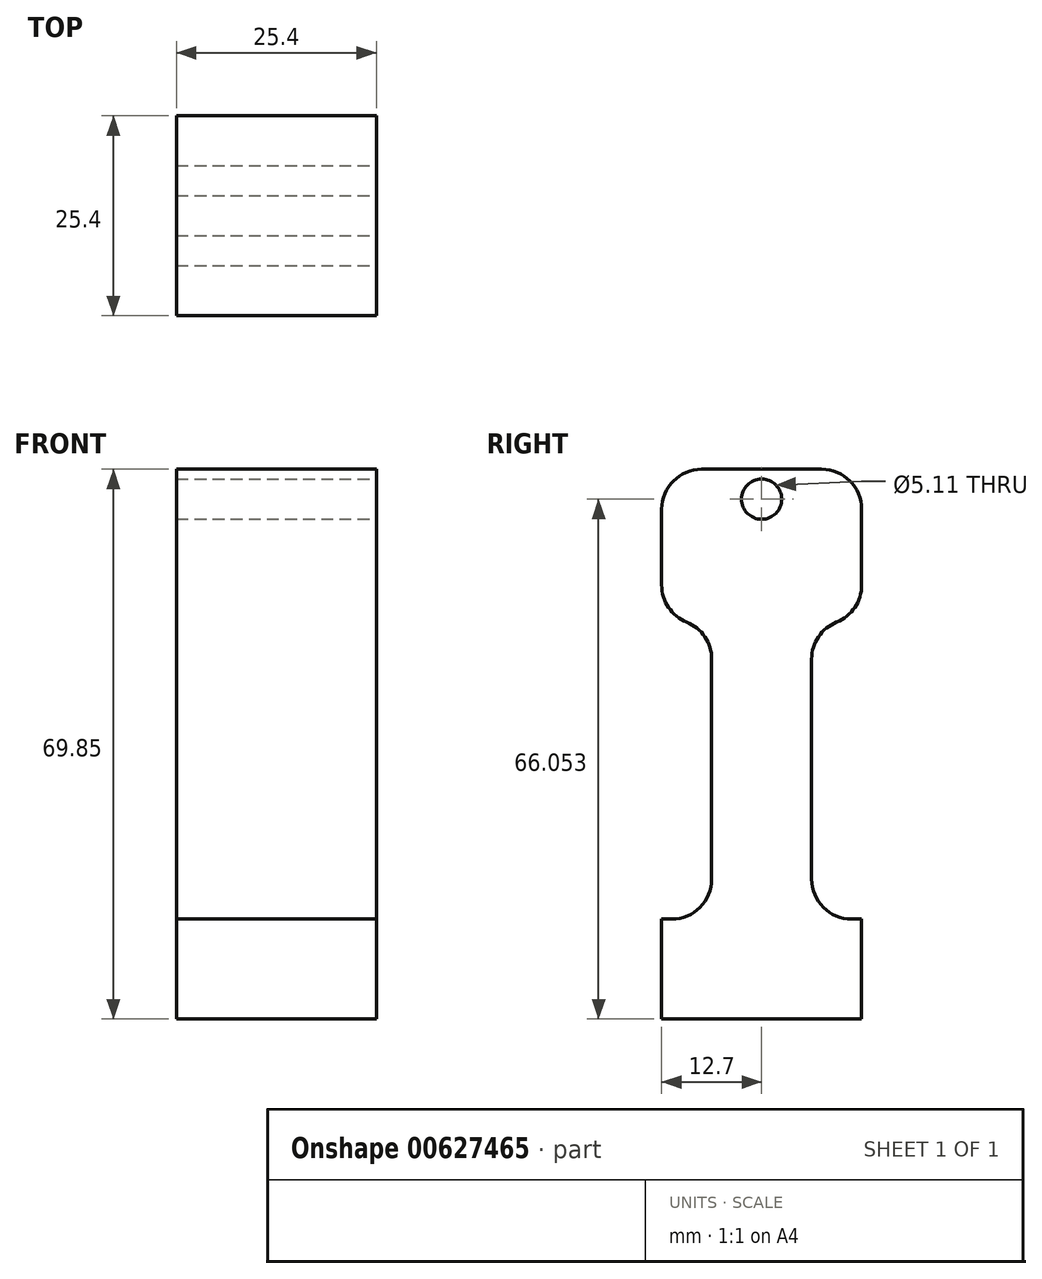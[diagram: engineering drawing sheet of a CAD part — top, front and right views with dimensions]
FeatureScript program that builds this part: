
annotation { "Feature Type Name" : "Feature", "Feature Type Description" : "" }
export const myFeature = defineFeature(function(context is Context, id is Id, definition is map)
    precondition{}
    {
        {
            var Q0;
            Q0=qCreatedBy(makeId("Top.planeOp"),FACE);
            var sketch = newSketch(context, id + "F0", { "sketchPlane" : qUnion([Q0])});
            skLineSegment(sketch, "E0.bottom", {"start": v(12.7, 12.7) * mm, "end": v(-12.7, 12.7) * mm});
            skLineSegment(sketch, "E0.top", {"start": v(12.7, -12.7) * mm, "end": v(-12.7, -12.7) * mm});
            skLineSegment(sketch, "E0.left", {"start": v(12.7, 12.7) * mm, "end": v(12.7, -12.7) * mm});
            skLineSegment(sketch, "E0.right", {"start": v(-12.7, 12.7) * mm, "end": v(-12.7, -12.7) * mm});
            skPoint(sketch, "E0.middle", {"position": v(0, 0) * mm});
            skSolve(sketch);
        }
        {
            var Q0;
            Q0 = qSketchRegion(id + "F0", true);
            extrude(context, id + "F1", {"entities" : qUnion([Q0]), "depth" : 69.85 * mm, "offsetDistance" : 25.4 * mm});
        }
        {
            var Q0;
            Q0=makeQuery(id+"F1.opExtrude","SWEPT_FACE",FACE,{"disambiguationData":[OSD([sQuery(id+"F0.wireOp",EDGE,"E0.left")])]});
            var sketch = newSketch(context, id + "F2", { "sketchPlane" : qUnion([Q0])});
            skCircle(sketch, "E1", {"center": v(0, 66.05) * mm, "radius": 2.55 * mm});
            skSolve(sketch);
        }
        {
            var Q0;
            Q0=makeQuery(id+"F2.imprint","IMPRINT",FACE,{"disambiguationData":[TD([[makeQuery(id+"F2.imprint","IMPRINT",EDGE,{"derivedFrom":sQuery(id+"F2.wireOp",EDGE,"E1")}),1.0]])]});
            extrude(context, id + "F3", {"entities" : qUnion([Q0]), "operationType" : NewBodyOperationType.REMOVE, "oppositeDirection" : true, "depth" : 25.4 * mm, "offsetDistance" : 25.4 * mm});
        }
        {
            var Q0;
            Q0=makeQuery(id+"F1.opExtrude","CAP_EDGE",EDGE,{"disambiguationData":[OSD([sQuery(id+"F0.wireOp",EDGE,"E0.top")])],"isStart":false});
            var Q1;
            Q1=makeQuery(id+"F1.opExtrude","CAP_EDGE",EDGE,{"disambiguationData":[OSD([sQuery(id+"F0.wireOp",EDGE,"E0.bottom")])],"isStart":false});
            fillet(context, id + "F4", {"entities" : qUnion([Q0, Q1]), "radius" : 5.08 * mm, "tangentPropagation" : true, "allowEdgeOverflow" : false});
        }
        {
            var Q0;
            Q0=makeQuery(id+"F1.opExtrude","SWEPT_FACE",FACE,{"disambiguationData":[OSD([sQuery(id+"F0.wireOp",EDGE,"E0.left")])]});
            var sketch = newSketch(context, id + "F5", { "sketchPlane" : qUnion([Q0])});
            skLineSegment(sketch, "E2.bottom", {"start": v(-12.7, 12.7) * mm, "end": v(-6.35, 12.7) * mm});
            skLineSegment(sketch, "E2.top", {"start": v(-12.7, 50.8) * mm, "end": v(-6.35, 50.8) * mm});
            skLineSegment(sketch, "E2.left", {"start": v(-12.7, 12.7) * mm, "end": v(-12.7, 50.8) * mm});
            skLineSegment(sketch, "E2.right", {"start": v(-6.35, 12.7) * mm, "end": v(-6.35, 50.8) * mm});
            skLineSegment(sketch, "E3.bottom", {"start": v(12.7, 12.7) * mm, "end": v(6.35, 12.7) * mm});
            skLineSegment(sketch, "E3.top", {"start": v(12.7, 50.8) * mm, "end": v(6.35, 50.8) * mm});
            skLineSegment(sketch, "E3.left", {"start": v(12.7, 12.7) * mm, "end": v(12.7, 50.8) * mm});
            skLineSegment(sketch, "E3.right", {"start": v(6.35, 12.7) * mm, "end": v(6.35, 50.8) * mm});
            skSolve(sketch);
        }
        {
            var Q0;
            Q0 = qSketchRegion(id + "F5", true);
            extrude(context, id + "F6", {"entities" : qUnion([Q0]), "operationType" : NewBodyOperationType.REMOVE, "oppositeDirection" : true, "depth" : 25.4 * mm, "offsetDistance" : 25.4 * mm});
        }
        {
            var Q0;
            Q0=makeQuery(id+"F6.boolean.opBoolean","COPY",EDGE,{"derivedFrom":makeQuery(id+"F6.opExtrude","SWEPT_EDGE",EDGE,{"disambiguationData":[OSD([sQuery(id+"F5.wireOp",EDGE,"E3.top"),sQuery(id+"F5.wireOp",EDGE,"E3.right")])]})});
            var Q1;
            Q1=makeQuery(id+"F6.boolean.opBoolean","COPY",EDGE,{"derivedFrom":makeQuery(id+"F6.opExtrude","SWEPT_EDGE",EDGE,{"disambiguationData":[OSD([sQuery(id+"F5.wireOp",EDGE,"E3.bottom"),sQuery(id+"F5.wireOp",EDGE,"E3.right")])]})});
            var Q2;
            Q2=makeQuery(id+"F6.boolean.opBoolean","COPY",EDGE,{"derivedFrom":makeQuery(id+"F6.opExtrude","SWEPT_EDGE",EDGE,{"disambiguationData":[OSD([sQuery(id+"F5.wireOp",EDGE,"E2.top"),sQuery(id+"F5.wireOp",EDGE,"E2.right")])]})});
            var Q3;
            Q3=makeQuery(id+"F6.boolean.opBoolean","COPY",EDGE,{"derivedFrom":makeQuery(id+"F6.opExtrude","SWEPT_EDGE",EDGE,{"disambiguationData":[OSD([sQuery(id+"F5.wireOp",EDGE,"E2.bottom"),sQuery(id+"F5.wireOp",EDGE,"E2.right")])]})});
            fillet(context, id + "F7", {"entities" : qUnion([Q0, Q1, Q2, Q3]), "radius" : 5.08 * mm, "tangentPropagation" : true, "allowEdgeOverflow" : false});
        }
        {
            var Q0;
            Q0=makeQuery(id+"F6.boolean.opBoolean","COPY",EDGE,{"derivedFrom":makeQuery(id+"F6.opExtrude","SWEPT_EDGE",EDGE,{"disambiguationData":[OSD([sQuery(id+"F0.wireOp",EDGE,"E0.top"),sQuery(id+"F0.wireOp",EDGE,"E0.left"),sQuery(id+"F5.wireOp",EDGE,"E2.bottom"),sQuery(id+"F5.wireOp",EDGE,"E2.left")])]})});
            var Q1;
            Q1=makeQuery(id+"F6.boolean.opBoolean","COPY",EDGE,{"derivedFrom":makeQuery(id+"F6.opExtrude","SWEPT_EDGE",EDGE,{"disambiguationData":[OSD([sQuery(id+"F0.wireOp",EDGE,"E0.top"),sQuery(id+"F0.wireOp",EDGE,"E0.left"),sQuery(id+"F5.wireOp",EDGE,"E2.top"),sQuery(id+"F5.wireOp",EDGE,"E2.left")])]})});
            var Q2;
            Q2=makeQuery(id+"F6.boolean.opBoolean","COPY",EDGE,{"derivedFrom":makeQuery(id+"F6.opExtrude","SWEPT_EDGE",EDGE,{"disambiguationData":[OSD([sQuery(id+"F0.wireOp",EDGE,"E0.bottom"),sQuery(id+"F0.wireOp",EDGE,"E0.left"),sQuery(id+"F5.wireOp",EDGE,"E3.bottom"),sQuery(id+"F5.wireOp",EDGE,"E3.left")])]})});
            var Q3;
            Q3=makeQuery(id+"F6.boolean.opBoolean","COPY",EDGE,{"derivedFrom":makeQuery(id+"F6.opExtrude","SWEPT_EDGE",EDGE,{"disambiguationData":[OSD([sQuery(id+"F0.wireOp",EDGE,"E0.bottom"),sQuery(id+"F0.wireOp",EDGE,"E0.left"),sQuery(id+"F5.wireOp",EDGE,"E3.top"),sQuery(id+"F5.wireOp",EDGE,"E3.left")])]})});
            fillet(context, id + "F8", {"entities" : qUnion([Q0, Q1, Q2, Q3]), "radius" : 5.08 * mm, "tangentPropagation" : true, "allowEdgeOverflow" : false});
        }
    });
